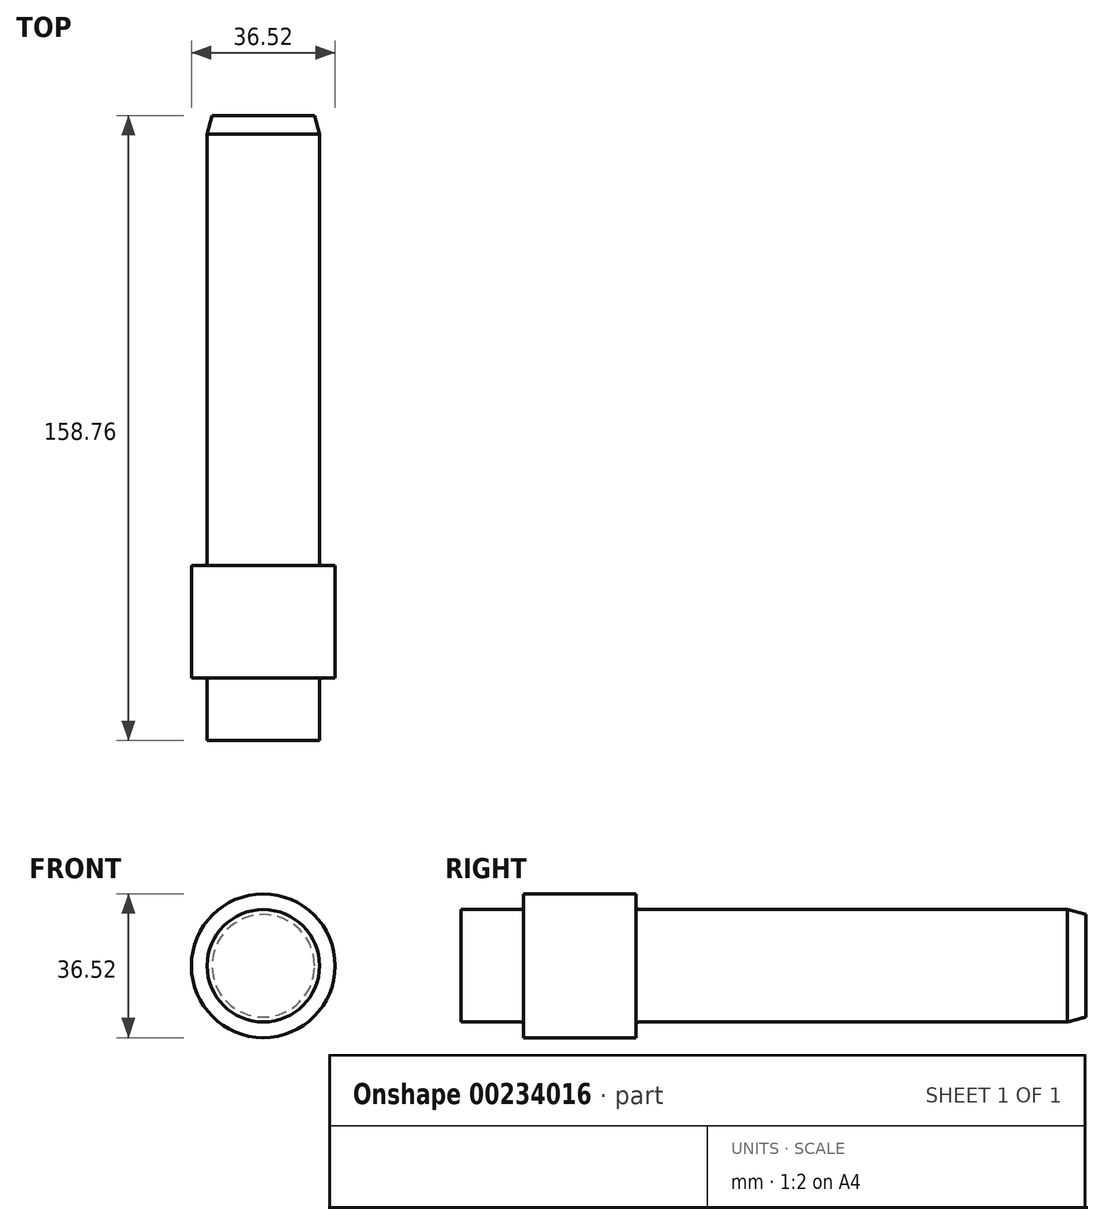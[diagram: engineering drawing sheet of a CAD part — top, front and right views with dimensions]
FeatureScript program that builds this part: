
annotation { "Feature Type Name" : "Feature", "Feature Type Description" : "" }
export const myFeature = defineFeature(function(context is Context, id is Id, definition is map)
    precondition{}
    {
        {
            var Q0;
            Q0=qCreatedBy(makeId("Right.planeOp"),FACE);
            var sketch = newSketch(context, id + "F0", { "sketchPlane" : qUnion([Q0])});
            skLineSegment(sketch, "E0", {"start": v(-15.88, 0) * mm, "end": v(142.88, 0) * mm});
            skLineSegment(sketch, "E1", {"start": v(142.88, 0) * mm, "end": v(142.88, 13.01) * mm});
            skLineSegment(sketch, "E2", {"start": v(142.88, 13.01) * mm, "end": v(138.11, 14.29) * mm});
            skLineSegment(sketch, "E3", {"start": v(138.11, 14.29) * mm, "end": v(28.58, 14.29) * mm});
            skLineSegment(sketch, "E4", {"start": v(28.58, 14.29) * mm, "end": v(28.58, 18.26) * mm});
            skLineSegment(sketch, "E5", {"start": v(28.58, 18.26) * mm, "end": v(0, 18.26) * mm});
            skLineSegment(sketch, "E6", {"start": v(0, 18.26) * mm, "end": v(0, 14.29) * mm});
            skLineSegment(sketch, "E7", {"start": v(0, 14.29) * mm, "end": v(-15.88, 14.29) * mm});
            skLineSegment(sketch, "E8", {"start": v(-15.88, 14.29) * mm, "end": v(-15.88, 0) * mm});
            skSolve(sketch);
        }
        {
            var Q0;
            Q0=makeQuery(id+"F0.imprint","IMPRINT",FACE,{"disambiguationData":[TD([[makeQuery(id+"F0.imprint","IMPRINT",EDGE,{"derivedFrom":sQuery(id+"F0.wireOp",EDGE,"E0")}),1.0]])]});
            var Q1;
            Q1=sQuery(id+"F0.wireOp",EDGE,"E0");
            revolve(context, id + "F1", {"entities" : qUnion([Q0]), "axis" : qUnion([Q1]), "revolveType" : RevolveType.FULL});
        }
        {
            var Q0;
            Q0=makeQuery(id+"F1.opRevolve","SWEPT_EDGE",EDGE,{"disambiguationData":[OSD([sQuery(id+"F0.wireOp",EDGE,"E6"),sQuery(id+"F0.wireOp",EDGE,"E7")])]});
            fillet(context, id + "F2", {"entities" : qUnion([Q0]), "radius" : 0.8 * mm, "tangentPropagation" : true, "allowEdgeOverflow" : false});
        }
        {
            var Q0;
            Q0=makeQuery(id+"F1.opRevolve","SWEPT_EDGE",EDGE,{"disambiguationData":[OSD([sQuery(id+"F0.wireOp",EDGE,"E3"),sQuery(id+"F0.wireOp",EDGE,"E4")])]});
            fillet(context, id + "F3", {"entities" : qUnion([Q0]), "radius" : 0.8 * mm, "tangentPropagation" : true, "allowEdgeOverflow" : false});
        }
    });
